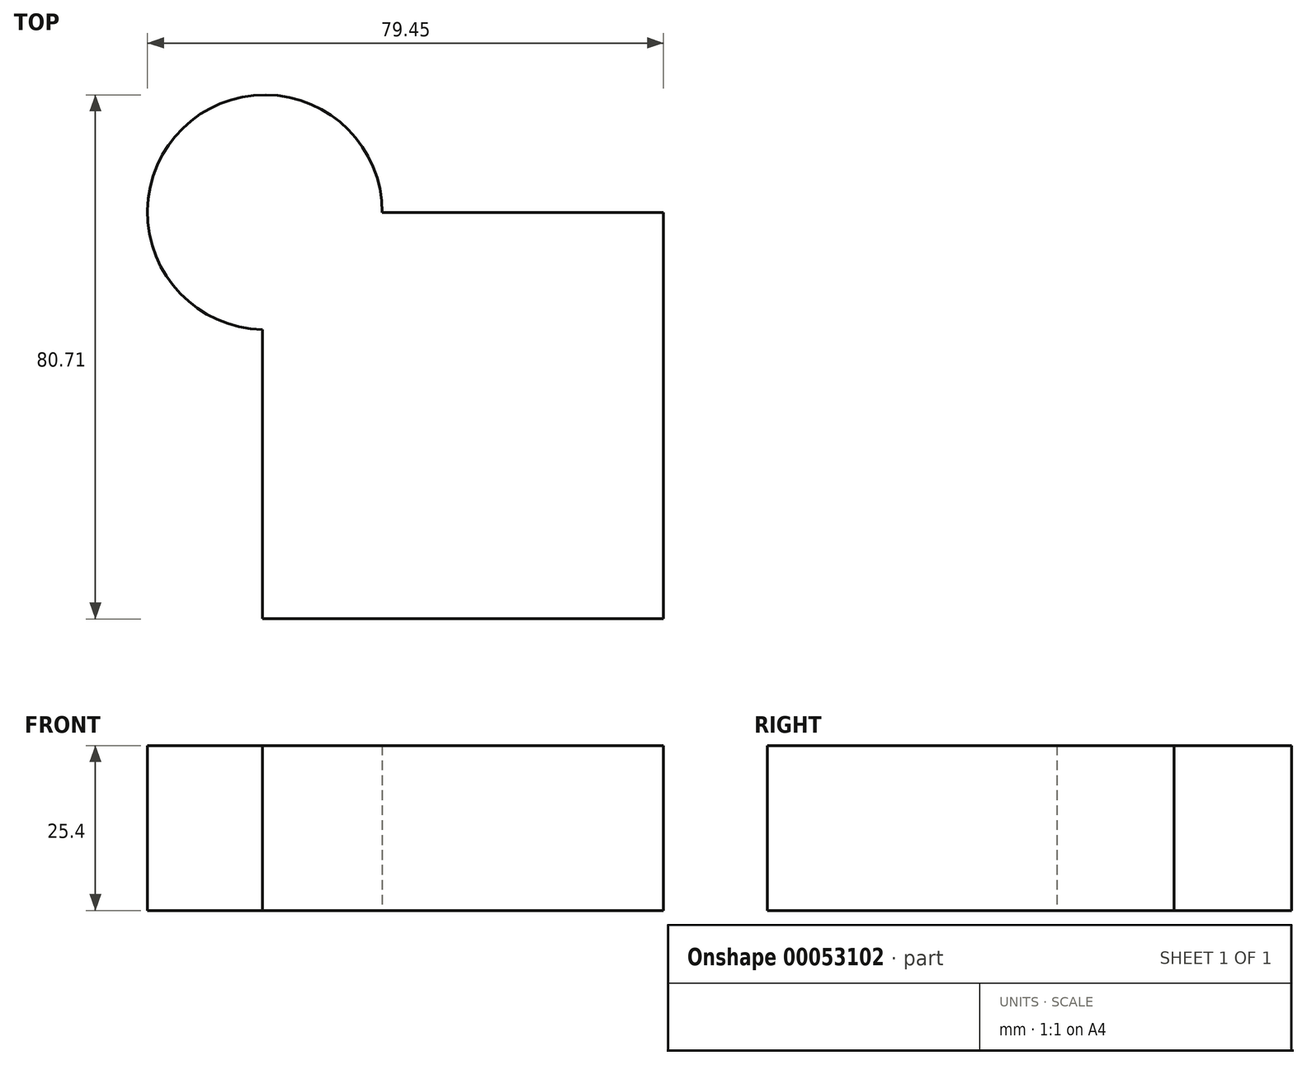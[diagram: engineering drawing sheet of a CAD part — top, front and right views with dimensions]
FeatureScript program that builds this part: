
annotation { "Feature Type Name" : "Feature", "Feature Type Description" : "" }
export const myFeature = defineFeature(function(context is Context, id is Id, definition is map)
    precondition{}
    {
        {
            var Q0;
            Q0=qCreatedBy(makeId("Top.planeOp"),FACE);
            var sketch = newSketch(context, id + "F0", { "sketchPlane" : qUnion([Q0])});
            skLineSegment(sketch, "E0.bottom", {"start": v(-31.97, -24.49) * mm, "end": v(29.78, -24.49) * mm});
            skLineSegment(sketch, "E0.top", {"start": v(-13.53, 38.12) * mm, "end": v(29.78, 38.12) * mm});
            skLineSegment(sketch, "E0.left", {"start": v(-31.97, -24.49) * mm, "end": v(-31.97, 20.08) * mm});
            skLineSegment(sketch, "E0.right", {"start": v(29.78, -24.49) * mm, "end": v(29.78, 38.12) * mm});
            skArc(sketch, "E1", {"start": v(-13.53, 38.12) * mm, "mid": v(-44.24, 51.07) * mm, "end": v(-31.97, 20.08) * mm});
            skSolve(sketch);
        }
        {
            var Q0;
            Q0=makeQuery(id+"F0.imprint","IMPRINT",FACE,{"disambiguationData":[TD([[makeQuery(id+"F0.imprint","IMPRINT",EDGE,{"derivedFrom":sQuery(id+"F0.wireOp",EDGE,"E0.bottom")}),1.0]])]});
            extrude(context, id + "F1", {"entities" : qUnion([Q0]), "depth" : 25.4 * mm});
        }
    });
